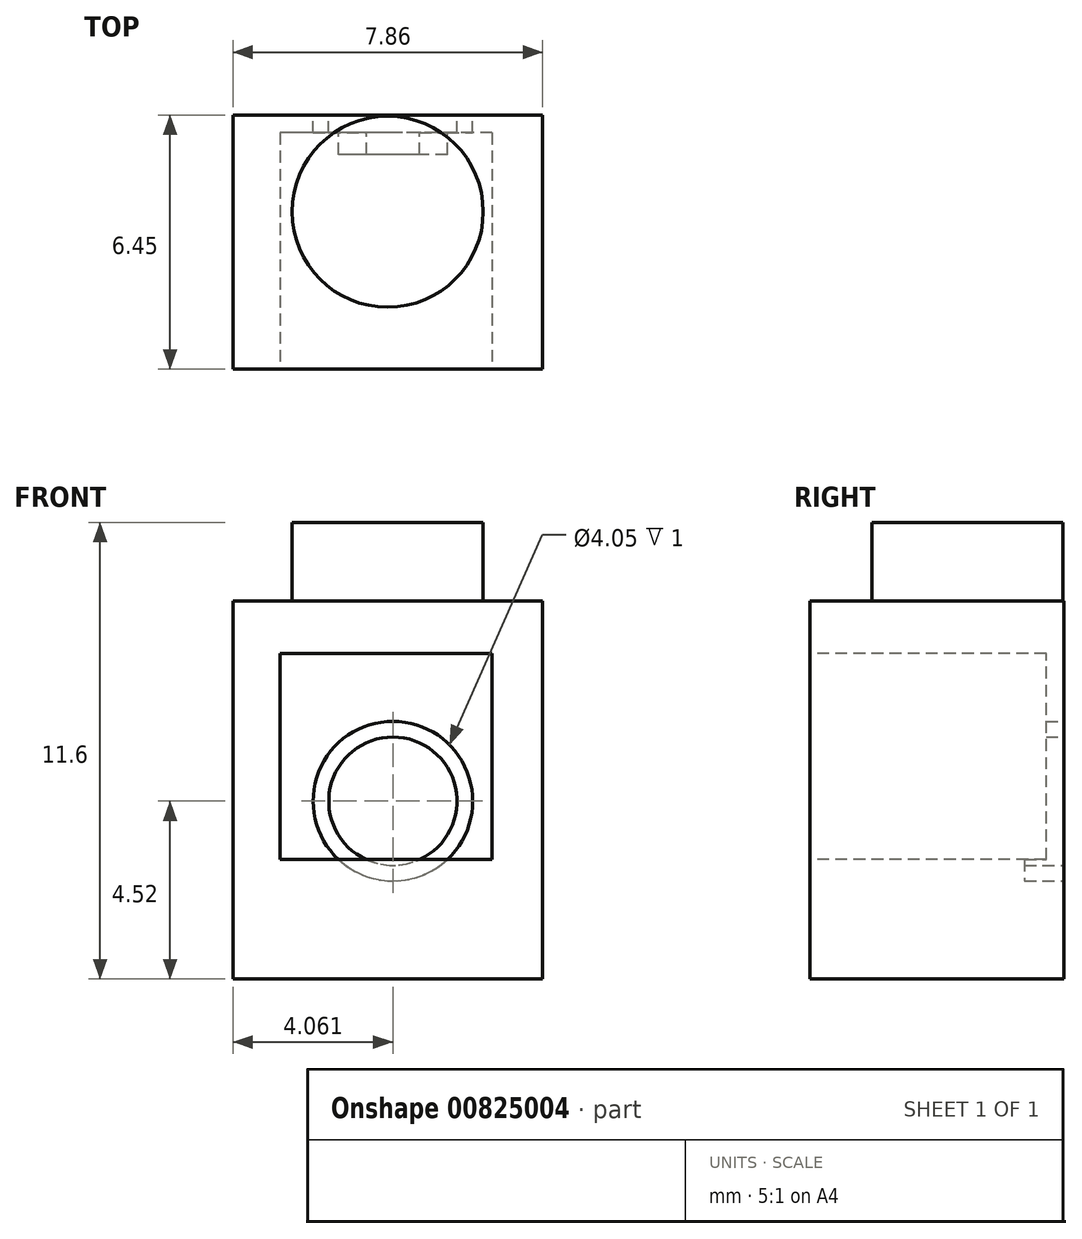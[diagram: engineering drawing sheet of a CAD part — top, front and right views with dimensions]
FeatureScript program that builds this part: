
annotation { "Feature Type Name" : "Feature", "Feature Type Description" : "" }
export const myFeature = defineFeature(function(context is Context, id is Id, definition is map)
    precondition{}
    {
        {
            var Q0;
            Q0=qCreatedBy(makeId("Top.planeOp"),FACE);
            var sketch = newSketch(context, id + "F0", { "sketchPlane" : qUnion([Q0])});
            skLineSegment(sketch, "E0", {"start": v(-59.05, 48.37) * mm, "end": v(-51.2, 48.37) * mm});
            skLineSegment(sketch, "E1", {"start": v(-51.2, 48.37) * mm, "end": v(-51.2, 41.92) * mm});
            skLineSegment(sketch, "E2", {"start": v(-51.2, 41.92) * mm, "end": v(-59.05, 41.92) * mm});
            skLineSegment(sketch, "E3", {"start": v(-59.05, 41.92) * mm, "end": v(-59.05, 48.37) * mm});
            skSolve(sketch);
        }
        {
            var Q0;
            Q0 = qSketchRegion(id + "F0", true);
            extrude(context, id + "F1", {"entities" : qUnion([Q0]), "depth" : 9.6 * mm, "offsetDistance" : 25 * mm});
        }
        {
            var Q0;
            Q0=makeQuery(id+"F1.opExtrude","CAP_FACE",FACE,{"disambiguationData":[OSD([sQuery(id+"F0.wireOp",EDGE,"E0"),sQuery(id+"F0.wireOp",EDGE,"E1"),sQuery(id+"F0.wireOp",EDGE,"E2"),sQuery(id+"F0.wireOp",EDGE,"E3")])],"isStart":false});
            var sketch = newSketch(context, id + "F2", { "sketchPlane" : qUnion([Q0])});
            skCircle(sketch, "E4", {"center": v(-55.12, 45.92) * mm, "radius": 2.43 * mm});
            skSolve(sketch);
        }
        {
            var Q0;
            Q0 = qSketchRegion(id + "F2", true);
            extrude(context, id + "F3", {"entities" : qUnion([Q0]), "operationType" : NewBodyOperationType.ADD, "depth" : 2 * mm, "offsetDistance" : 25 * mm});
        }
        {
            var Q0;
            Q0=makeQuery(id+"F1.opExtrude","SWEPT_FACE",FACE,{"disambiguationData":[OSD([sQuery(id+"F0.wireOp",EDGE,"E2")])]});
            var sketch = newSketch(context, id + "F4", { "sketchPlane" : qUnion([Q0])});
            skLineSegment(sketch, "E5.bottom", {"start": v(-52.47, 3.04) * mm, "end": v(-57.85, 3.04) * mm});
            skLineSegment(sketch, "E5.top", {"start": v(-52.47, 8.27) * mm, "end": v(-57.85, 8.27) * mm});
            skLineSegment(sketch, "E5.left", {"start": v(-52.47, 3.04) * mm, "end": v(-52.47, 8.27) * mm});
            skLineSegment(sketch, "E5.right", {"start": v(-57.85, 3.04) * mm, "end": v(-57.85, 8.27) * mm});
            skSolve(sketch);
        }
        {
            var Q0;
            Q0 = qSketchRegion(id + "F4", true);
            extrude(context, id + "F5", {"entities" : qUnion([Q0]), "operationType" : NewBodyOperationType.REMOVE, "oppositeDirection" : true, "depth" : 6 * mm, "offsetDistance" : 25 * mm});
        }
        {
            var Q0;
            Q0=makeQuery(id+"F1.opExtrude","SWEPT_FACE",FACE,{"disambiguationData":[OSD([sQuery(id+"F0.wireOp",EDGE,"E0")])]});
            var sketch = newSketch(context, id + "F6", { "sketchPlane" : qUnion([Q0])});
            skCircle(sketch, "E6", {"center": v(54.99, 4.52) * mm, "radius": 1.63 * mm});
            skCircle(sketch, "E7", {"center": v(54.99, 4.52) * mm, "radius": 2.03 * mm});
            skSolve(sketch);
        }
        {
            var Q0;
            Q0 = qSketchRegion(id + "F6", true);
            extrude(context, id + "F7", {"entities" : qUnion([Q0]), "operationType" : NewBodyOperationType.REMOVE, "oppositeDirection" : true, "depth" : 1 * mm, "offsetDistance" : 25 * mm});
        }
    });
